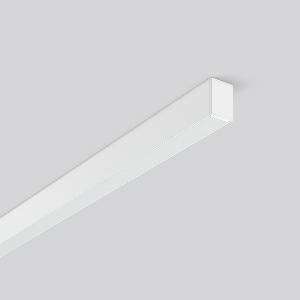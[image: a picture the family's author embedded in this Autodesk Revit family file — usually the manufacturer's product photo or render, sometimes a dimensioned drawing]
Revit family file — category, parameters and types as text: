
# Revit family: less_is_more_27_312198_002_76_3622
name_source: partatom
category: Lighting Fixtures
units: mm (PartAtom-declared; Revit-internal decimal feet)

## family parameters
Cut with Voids When Loaded = No
Host = Face
Light Source = No
Part Type = Normal
Room Calculation Point = No
Round Connector Dimension = Use Diameter
Shared = No

## types (1)
- LESS IS MORE 27 (1 x LED Modul 830, 2350 lm, 3000)
    Apparent Load = 35 VA
    CIE Flux Codes = 48 79 96 100 100
    Color Rendering = 80
    Color Temperature = 3000
    Default Elevation = 1800 mm
    Description = Series: LESS IS MORE 27
Ceiling and wall luminaire with slim design. Housing: extruded aluminium profile, powder-coated. End cap aluminium powder-coated. Diffuser made of non-yellowing plastic (PMMA), opal. Suitable for Ceiling mounting, Wall (surface). External driver with connecting cable. 
Colour: traffic white, matt (RAL 9016)
Length: 1212 mm
Width: 28 mm
Height: 38 mm
Lamp: LED
Socket: without socket
Colour temperature: 3000K
Colour rendering index (CRI): 82
System power: 35 W
Rated luminous flux: 2350 lm
Luminous efficiency: 67 lm/W
Control gear: Voltage converter, DALI dim.
Protection class: II
Type of protection: IP 20
    Height = 38 mm
    Lamp = 1 x LED Modul 830
    Lamp Light Flux = 2350 lm
    Lamp count = 1
    Length = 1212 mm
    Lifetime = 50000 h
    Luminous efficacy = 67 lm/W
    Manufacturer = RZB
    ModVariant = No
    Model = 312198.002.76
    Mounting Place = Ceiling, Wall
    Mounting Type = Surface mounted
    Number of Poles = 1
    OnlyDefault = Yes
    Power Factor = 1
    Product Name = LESS IS MORE 27
    Product group = Surface mounted LED linear luminaires
    ProductGroupID = 307
    Protection Class = Protection class II
    Protection Degree = IP 20
    RLX_Detail_Level = 1
    RLX_Emergency_Light_Flux = 0 lm
    RLX_Emergency_Type = 0
    RLX_Emergency_Type_DB = No
    RlxData = <blob elided: 22777 chars, md5=e8957bca>
    Socket = socket
    Standby Power = 0 W
    System Light Flux = 2350 lm
    System Power = 35 W
    Type Comments = Product without accessories
    Type Image = 312196.002.jpg
    URL = http://relux.com
    VarID = ---
    Voltage = 230 V
    Voltage Range = 220-240 V
    Weight = 0.00 kg
    Width = 28 mm

## geometry (parser evidence)
native form markers: Blend x4, Sweep x12
no freeform markers — native parametric forms only
